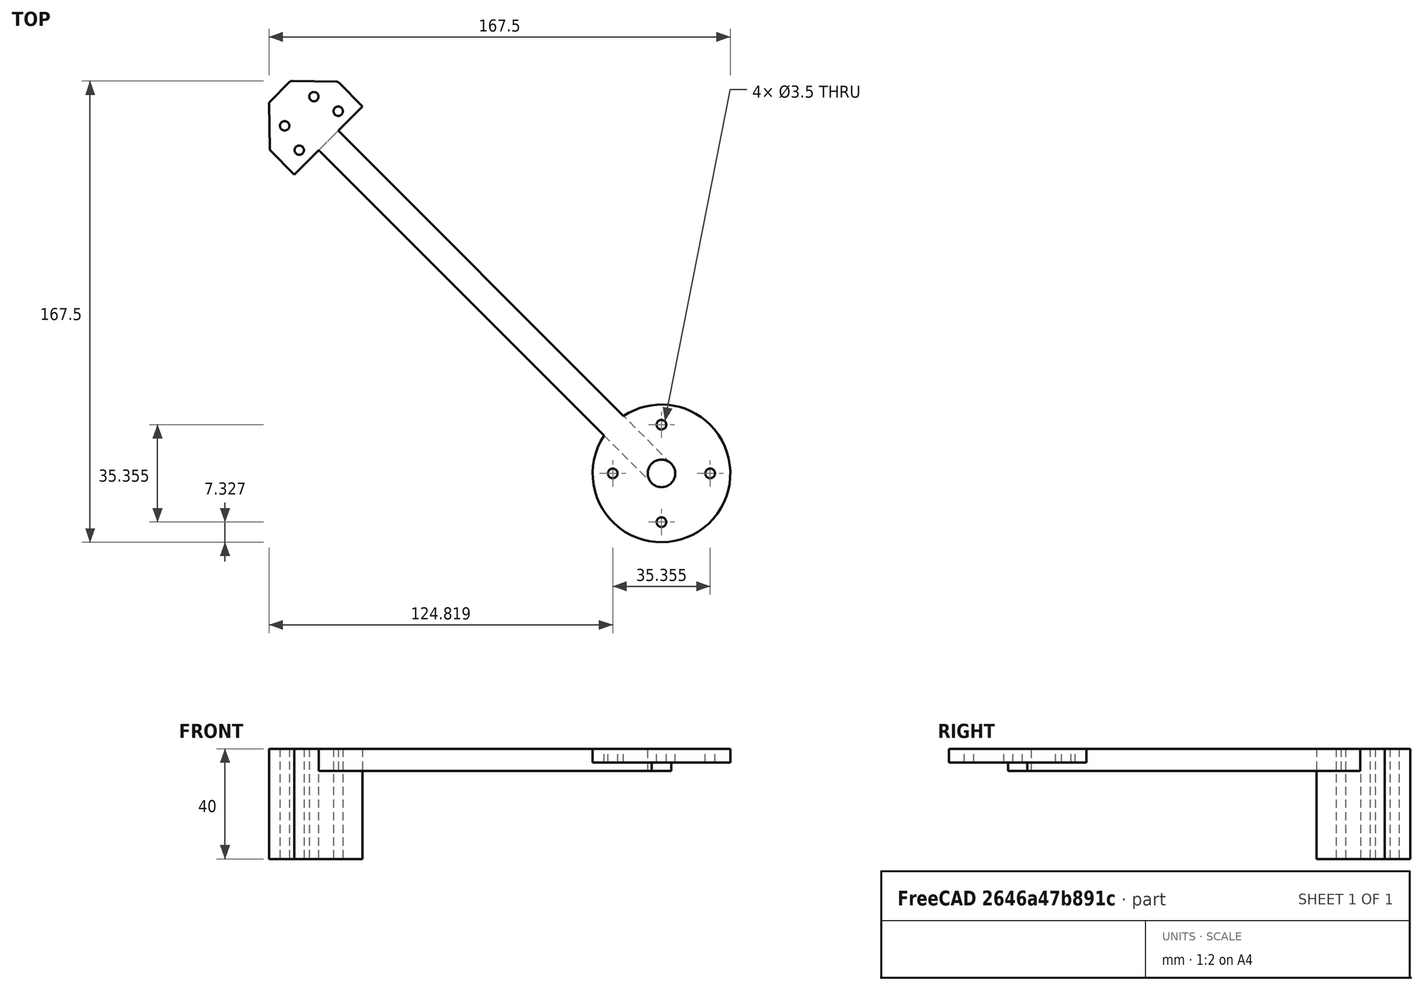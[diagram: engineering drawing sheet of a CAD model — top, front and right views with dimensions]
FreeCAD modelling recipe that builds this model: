
FCSTD DOCUMENT  (FreeCAD 1.0R39285 (Git))
Label: rr-middle-body_test
License: All rights reserved
LicenseURL: http://en.wikipedia.org/wiki/All_rights_reserved
objects: Sketcher::SketchObject×4, Spreadsheet::Sheet×1, Part::FeaturePython×1, PartDesign::Body×1
note: 10 computed .brp shape members not serialized (recipe doc carries the construction recipe); baked Part::Feature solids carry a one-line shape summary decoded from their .brp

FEATURE [Spreadsheet::Sheet] Spreadsheet
  cells = A1='offset_x; B1(offset_x)=15; A2='offset_y; B2(offset_y)=15; A3='base_x; B3(base_x)=170; A4='base_y; B4(base_y)=180; A5='base_h; B5(base_h)=183.5
FEATURE [Part::FeaturePython] b_leg_001_  label="leg_Body_001"  # a2plus imported part (geometry in sourceFile) (typed FeaturePython)
  Placement = pos=(281.203,-177.571,0) rot=(0,0,1;0.785398rad)
  a2p_Version = 0.4.68
  fixedPosition = true
  objectType = a2pPart
  sourceFile = ./leg.FCStd
  sourcePart = Body
  subassemblyImport = false
  timeLastImport = 1.75319e+09
  updateColors = true
FEATURE [Sketcher::SketchObject] Sketch  label="base_plate"
  ArcFitTolerance = 1e-06
  AttachmentSupport = -> [XY_Plane]
  FullyConstrained = true
  MakeInternals = false
  MapMode = 5
  expr: Constraints[12] = Spreadsheet.offset_y
  expr: Constraints[13] = Spreadsheet.offset_x
  expr: Constraints[18] = Spreadsheet.offset_x
  expr: Constraints[22] = Spreadsheet.base_x
  expr: Constraints[23] = Spreadsheet.base_y
  sketch-geometry (8):
    g0: LineSegment StartX=15 StartY=39.7487 StartZ=0 EndX=39.7487 EndY=15 EndZ=0
    g1: LineSegment StartX=39.7487 StartY=15 StartZ=0 EndX=160.251 EndY=15 EndZ=0
    g2: LineSegment StartX=160.251 StartY=15 StartZ=0 EndX=185 EndY=39.7487 EndZ=0
    g3: LineSegment StartX=185 StartY=39.7487 StartZ=0 EndX=185 EndY=170.251 EndZ=0
    g4: LineSegment StartX=185 StartY=170.251 StartZ=0 EndX=160.251 EndY=195 EndZ=0
    g5: LineSegment StartX=160.251 StartY=195 StartZ=0 EndX=39.7487 EndY=195 EndZ=0
    g6: LineSegment StartX=39.7487 StartY=195 StartZ=0 EndX=15 EndY=170.251 EndZ=0
    g7: LineSegment StartX=15 StartY=170.251 StartZ=0 EndX=15 EndY=39.7487 EndZ=0
  constraints (24):
    c: Coincident(g0,g1)
    c: Horizontal(g1)
    c: Coincident(g1,g2)
    c: Coincident(g2,g3)
    c: Vertical(g3)
    c: Coincident(g3,g4)
    c: Coincident(g4,g5)
    c: Horizontal(g5)
    c: Coincident(g5,g6)
    c: Coincident(g6,g7)
    c: Coincident(g7,g0)
    c: Distance(g0,g0) = 35
    c: DistanceY(g-1,g0) = 15
    c: DistanceX(g-1,g6) = 15
    c: Angle(g1,g0) = 2.35619
    c: Equal(g0,g6)
    c: Equal(g6,g4)
    c: Equal(g4,g2)
    c: DistanceX(g-1,g0) = 15
    c: Horizontal(g2,g0)
    c: Horizontal(g6,g3)
    c: Vertical(g5,g0)
    c: DistanceX(g0,g2) = 170
    c: DistanceY(g0,g5) = 180
FEATURE [Sketcher::SketchObject] Sketch001  label="engine_arm_holes"
  ArcFitTolerance = 1e-06
  AttachmentSupport = -> [XY_Plane]
  FullyConstrained = true
  MakeInternals = false
  MapMode = 5
  expr: Constraints[13] = Spreadsheet.base_x - 47
  expr: Constraints[21] = Spreadsheet.base_h
  expr: Constraints[22] = Spreadsheet.base_h
  expr: Constraints[42] = Spreadsheet.base_h
  expr: Constraints[43] = Spreadsheet.base_h
  expr: Constraints[44] = 10
  sketch-geometry (16):
    g0: Circle CenterX=32.5993 CenterY=42.7041 CenterZ=0 NormalX=0 NormalY=0 NormalZ=1 AngleXU=0 Radius=1.5
    g1: Circle CenterX=43.5 CenterY=32.4 CenterZ=0 NormalX=0 NormalY=0 NormalZ=1 AngleXU=0 Radius=1.5
    g2: Circle CenterX=24 CenterY=37.6 CenterZ=0 NormalX=0 NormalY=0 NormalZ=1 AngleXU=0 Radius=1.5
    g3: Circle CenterX=38.1841 CenterY=23.5 CenterZ=0 NormalX=0 NormalY=0 NormalZ=1 AngleXU=0 Radius=1.5
    g4: Circle CenterX=161.184 CenterY=23.5 CenterZ=0 NormalX=0 NormalY=0 NormalZ=1 AngleXU=0 Radius=1.5
    g5: Circle CenterX=176.085 CenterY=36.8406 CenterZ=0 NormalX=0 NormalY=0 NormalZ=1 AngleXU=0 Radius=1.5
    g6: Circle CenterX=167.984 CenterY=42.7041 CenterZ=0 NormalX=0 NormalY=0 NormalZ=1 AngleXU=0 Radius=1.5
    g7: Circle CenterX=168.148 CenterY=167.067 CenterZ=0 NormalX=0 NormalY=0 NormalZ=1 AngleXU=0 Radius=1.5
    g8: Circle CenterX=157.247 CenterY=177.371 CenterZ=0 NormalX=0 NormalY=0 NormalZ=1 AngleXU=0 Radius=1.5
    g9: Circle CenterX=162.301 CenterY=186 CenterZ=0 NormalX=0 NormalY=0 NormalZ=1 AngleXU=0 Radius=1.5
    g10: Circle CenterX=176.748 CenterY=172.17 CenterZ=0 NormalX=0 NormalY=0 NormalZ=1 AngleXU=0 Radius=1.5
    g11: Circle CenterX=32.5993 CenterY=166.896 CenterZ=0 NormalX=0 NormalY=0 NormalZ=1 AngleXU=0 Radius=1.5
    g12: Circle CenterX=43.3361 CenterY=177.371 CenterZ=0 NormalX=0 NormalY=0 NormalZ=1 AngleXU=0 Radius=1.5
    g13: Circle CenterX=38.2829 CenterY=186 CenterZ=0 NormalX=0 NormalY=0 NormalZ=1 AngleXU=0 Radius=1.5
    g14: Circle CenterX=24 CenterY=172 CenterZ=0 NormalX=0 NormalY=0 NormalZ=1 AngleXU=0 Radius=1.5
    g15: Circle CenterX=157.247 CenterY=32.2293 CenterZ=0 NormalX=0 NormalY=0 NormalZ=1 AngleXU=0 Radius=1.5
  constraints (48):
    c: Equal(g1,g0)
    c: Equal(g0,g2)
    c: Equal(g2,g3)
    c: Distance(g3,g2) = 20
    c: Distance(g0,g1) = 15
    c: Radius(g2) = 1.5
    c: Distance(g2,g0) = 10
    c: DistanceY(g-1,g2) = 37.6
    c: DistanceX(g-1,g2) = 24
    c: DistanceY(g-1,g3) = 23.5
    c: DistanceY(g-1,g1) = 32.4
    c: DistanceX(g-1,g1) = 43.5
    c: Horizontal(g4,g3)
    c: DistanceX(g3,g4) = 123
    c: Horizontal(g0,g6)
    c: Distance(g4,g5) = 20
    c: Equal(g10,g8)
    c: Equal(g8,g9)
    c: Distance(g10,g9) = 20
    c: Distance(g7,g8) = 15
    c: Distance(g7,g10) = 10
    c: Distance(g1,g7) = 183.5
    c: Distance(g8,g0) = 183.5
    c: Distance(g8,g9) = 10
    c: Equal(g8,g12)
    c: Equal(g12,g13)
    c: Equal(g13,g11)
    c: Vertical(g2,g14)
    c: Vertical(g0,g11)
    c: Distance(g14,g13) = 20
    c: Distance(g11,g12) = 15
    c: Distance(g14,g11) = 10
    c: Distance(g13,g12) = 10
    c: DistanceY(g-1,g14) = 172
    c: DistanceY(g-1,g13) = 186
    c: Horizontal(g8,g12)
    c: Horizontal(g9,g13)
    c: Equal(g1,g4)
    c: Equal(g4,g15)
    c: Equal(g15,g5)
    c: Equal(g5,g6)
    c: Distance(g15,g6) = 15
    c: Distance(g11,g15) = 183.5
    c: Distance(g6,g12) = 183.5
    c: Distance(g5,g6) = 10
    c: Equal(g10,g7)
    c: Equal(g9,g1)
    c: Equal(g13,g14)
FEATURE [Sketcher::SketchObject] Sketch002  label="mounting_plate"
  ArcFitTolerance = 1e-06
  AttachmentSupport = -> [XY_Plane]
  FullyConstrained = true
  MakeInternals = false
  MapMode = 5
  expr: Constraints[11] = Spreadsheet.base_x - 33 * 2
  expr: Constraints[8] = Spreadsheet.offset_x + 25
  expr: Constraints[9] = Spreadsheet.offset_x + 33
  sketch-geometry (4):
    g0: LineSegment StartX=40 StartY=194.944 StartZ=0 EndX=48 EndY=186 EndZ=0
    g1: LineSegment StartX=48 StartY=186 StartZ=0 EndX=152 EndY=186 EndZ=0
    g2: LineSegment StartX=152 StartY=186 StartZ=0 EndX=160 EndY=194.944 EndZ=0
    g3: LineSegment StartX=160 StartY=194.944 StartZ=0 EndX=40 EndY=194.944 EndZ=0
  constraints (12):
    c: Coincident(g0,g1)
    c: Horizontal(g1)
    c: Coincident(g1,g2)
    c: Coincident(g2,g3)
    c: Coincident(g3,g0)
    c: Horizontal(g3)
    c: Distance(g0,g0) = 12
    c: Equal(g0,g2)
    c: DistanceX(g-1,g0) = 40
    c: DistanceX(g-1,g0) = 48
    c: DistanceY(g-1,g0) = 186
    c: DistanceX(g0,g1) = 104
FEATURE [Sketcher::SketchObject] Sketch003  label="cube_kore_mount"
  ArcFitTolerance = 1e-06
  AttachmentSupport = -> [XY_Plane]
  FullyConstrained = false
  MakeInternals = false
  MapMode = 5
  expr: Constraints[16] = Spreadsheet.offset_x + Spreadsheet.base_x / 2 - 30
  expr: Constraints[17] = (Spreadsheet.offset_x + Spreadsheet.base_x) / 2 - 30
  sketch-geometry (6):
    g0: Circle CenterX=70 CenterY=56.8795 CenterZ=0 NormalX=0 NormalY=0 NormalZ=1 AngleXU=0 Radius=1.6
    g1: Circle CenterX=130 CenterY=56.8795 CenterZ=0 NormalX=0 NormalY=0 NormalZ=1 AngleXU=0 Radius=1.6
    g2: Circle CenterX=70 CenterY=166.879 CenterZ=0 NormalX=0 NormalY=0 NormalZ=1 AngleXU=0 Radius=1.6
    g3: Circle CenterX=130 CenterY=166.879 CenterZ=0 NormalX=0 NormalY=0 NormalZ=1 AngleXU=0 Radius=1.6
    g4: Circle CenterX=70 CenterY=111.879 CenterZ=0 NormalX=0 NormalY=0 NormalZ=1 AngleXU=0 Radius=1.6
    g5: Circle CenterX=130 CenterY=93.8795 CenterZ=0 NormalX=0 NormalY=0 NormalZ=1 AngleXU=0 Radius=1.6
  constraints (18):
    c: DistanceX(g0,g1) = 60
    c: Diameter(g0) = 3.2
    c: Equal(g0,g1)
    c: DistanceY(g0,g2) = 110
    c: Vertical(g0,g2)
    c: Equal(g0,g2)
    c: Horizontal(g0,g1)
    c: Horizontal(g2,g3)
    c: Vertical(g3,g1)
    c: Equal(g3,g2)
    c: Vertical(g5,g3)
    c: DistanceY(g5,g3) = 73
    c: Equal(g5,g1)
    c: Vertical(g4,g2)
    c: DistanceY(g4,g2) = 55
    c: Equal(g4,g2)
    c: DistanceX(g-1,g0) = 70
    c: DistanceX(g-1,g0) = 62.5
FEATURE [PartDesign::Body] Body
  AllowCompound = false
  Group = -> [Sketch,Sketch001,Sketch002,Sketch003]
  Origin = -> Origin
